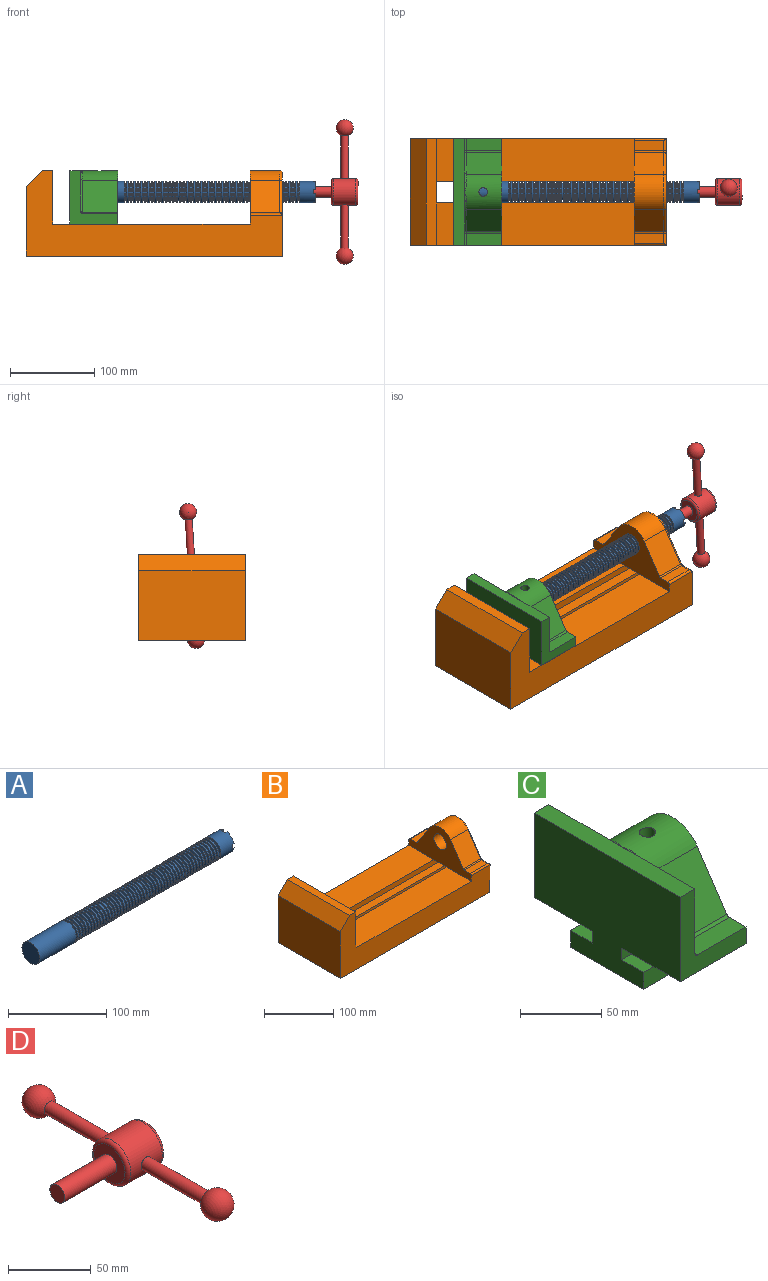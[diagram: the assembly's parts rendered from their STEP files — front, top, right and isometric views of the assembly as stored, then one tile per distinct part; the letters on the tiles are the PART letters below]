
ASSEMBLY  parts=4 mates=3
PART A: 220 faces, bbox 279.4x25.4x25.4 mm
  f0: cylinder r=12.7mm len=25.4mm, axis (-1,0,0), area 1468.2mm2, adj f1,f2,f3,f5,f7,f208,f209,f210
  f1: plane 9.9x9.9mm, normal (1,0,0), area 62.3mm2, adj f0,f4,f213,f216
  f2: plane 9.9x9.9mm, normal (1,0,0), area 62.3mm2, adj f0,f4,f210,f218
  f3: plane 9.9x9.9mm, normal (1,0,0), area 62.3mm2, adj f0,f4,f209,f212
  f4: cylinder r=6.35mm len=25.4mm, axis (1,0,0), area 960.3mm2, adj f1,f2,f3,f5,f6,f208,f209,f210
  f5: plane 9.9x9.9mm, normal (1,0,0), area 62.3mm2, adj f0,f4,f215,f217
  f6: plane 12.7x12.7mm, normal (1,0,0), area 126.7mm2, adj f4
  f7: cone r=12.7mm half-angle=76deg, axis (1,0,0), area 188mm2, adj f0,f9
  f8: cone r=10.16mm half-angle=76deg, axis (-1,0,0), area 188mm2, adj f9,f10
  f9: cylinder r=10.16mm len=20.32mm, axis (1,0,0), area 81.1mm2, adj f7,f8
  f10: cylinder r=12.7mm len=25.4mm, axis (-1,0,0), area 131.7mm2, adj f8,f11
  f11: cone r=12.7mm half-angle=76deg, axis (1,0,0), area 188mm2, adj f10,f13
  f12: cone r=10.16mm half-angle=76deg, axis (-1,0,0), area 188mm2, adj f13,f14
  f13: cylinder r=10.16mm len=20.32mm, axis (1,0,0), area 81.1mm2, adj f11,f12
  f14: cylinder r=12.7mm len=25.4mm, axis (-1,0,0), area 131.7mm2, adj f12,f15
  f15: cone r=12.7mm half-angle=76deg, axis (1,0,0), area 188mm2, adj f14,f17
  f16: cone r=10.16mm half-angle=76deg, axis (-1,0,0), area 188mm2, adj f17,f18
  f17: cylinder r=10.16mm len=20.32mm, axis (1,0,0), area 81.1mm2, adj f15,f16
  f18: cylinder r=12.7mm len=25.4mm, axis (-1,0,0), area 131.7mm2, adj f16,f19
  f19: cone r=12.7mm half-angle=76deg, axis (1,0,0), area 188mm2, adj f18,f21
  f20: cone r=10.16mm half-angle=76deg, axis (-1,0,0), area 188mm2, adj f21,f22
  f21: cylinder r=10.16mm len=20.32mm, axis (1,0,0), area 81.1mm2, adj f19,f20
  f22: cylinder r=12.7mm len=25.4mm, axis (-1,0,0), area 131.7mm2, adj f20,f23
  f23: cone r=12.7mm half-angle=76deg, axis (1,0,0), area 188mm2, adj f22,f25
  f24: cone r=10.16mm half-angle=76deg, axis (-1,0,0), area 188mm2, adj f25,f26
  f25: cylinder r=10.16mm len=20.32mm, axis (1,0,0), area 81.1mm2, adj f23,f24
  f26: cylinder r=12.7mm len=25.4mm, axis (-1,0,0), area 131.7mm2, adj f24,f27
  f27: cone r=12.7mm half-angle=76deg, axis (1,0,0), area 188mm2, adj f26,f29
  f28: cone r=10.16mm half-angle=76deg, axis (-1,0,0), area 188mm2, adj f29,f30
  f29: cylinder r=10.16mm len=20.32mm, axis (1,0,0), area 81.1mm2, adj f27,f28
  f30: cylinder r=12.7mm len=25.4mm, axis (-1,0,0), area 131.7mm2, adj f28,f31
  f31: cone r=12.7mm half-angle=76deg, axis (1,0,0), area 188mm2, adj f30,f33
  f32: cone r=10.16mm half-angle=76deg, axis (-1,0,0), area 188mm2, adj f33,f34
  f33: cylinder r=10.16mm len=20.32mm, axis (1,0,0), area 81.1mm2, adj f31,f32
  f34: cylinder r=12.7mm len=25.4mm, axis (-1,0,0), area 131.7mm2, adj f32,f35
  f35: cone r=12.7mm half-angle=76deg, axis (1,0,0), area 188mm2, adj f34,f37
  f36: cone r=10.16mm half-angle=76deg, axis (-1,0,0), area 188mm2, adj f37,f38
  f37: cylinder r=10.16mm len=20.32mm, axis (1,0,0), area 81.1mm2, adj f35,f36
  f38: cylinder r=12.7mm len=25.4mm, axis (-1,0,0), area 131.7mm2, adj f36,f39
  f39: cone r=12.7mm half-angle=76deg, axis (1,0,0), area 188mm2, adj f38,f41
  f40: cone r=10.16mm half-angle=76deg, axis (-1,0,0), area 188mm2, adj f41,f42
  f41: cylinder r=10.16mm len=20.32mm, axis (1,0,0), area 81.1mm2, adj f39,f40
  f42: cylinder r=12.7mm len=25.4mm, axis (-1,0,0), area 131.7mm2, adj f40,f43
  f43: cone r=12.7mm half-angle=76deg, axis (1,0,0), area 188mm2, adj f42,f45
  f44: cone r=10.16mm half-angle=76deg, axis (-1,0,0), area 188mm2, adj f45,f46
  f45: cylinder r=10.16mm len=20.32mm, axis (1,0,0), area 81.1mm2, adj f43,f44
  f46: cylinder r=12.7mm len=25.4mm, axis (-1,0,0), area 131.7mm2, adj f44,f47
  f47: cone r=12.7mm half-angle=76deg, axis (1,0,0), area 188mm2, adj f46,f49
  f48: cone r=10.16mm half-angle=76deg, axis (-1,0,0), area 188mm2, adj f49,f50
  f49: cylinder r=10.16mm len=20.32mm, axis (1,0,0), area 81.1mm2, adj f47,f48
  f50: cylinder r=12.7mm len=25.4mm, axis (-1,0,0), area 131.7mm2, adj f48,f51
  f51: cone r=12.7mm half-angle=76deg, axis (1,0,0), area 188mm2, adj f50,f53
  f52: cone r=10.16mm half-angle=76deg, axis (-1,0,0), area 188mm2, adj f53,f54
  f53: cylinder r=10.16mm len=20.32mm, axis (1,0,0), area 81.1mm2, adj f51,f52
  f54: cylinder r=12.7mm len=25.4mm, axis (-1,0,0), area 131.7mm2, adj f52,f55
  f55: cone r=12.7mm half-angle=76deg, axis (1,0,0), area 188mm2, adj f54,f57
  f56: cone r=10.16mm half-angle=76deg, axis (-1,0,0), area 188mm2, adj f57,f58
  f57: cylinder r=10.16mm len=20.32mm, axis (1,0,0), area 81.1mm2, adj f55,f56
  f58: cylinder r=12.7mm len=25.4mm, axis (-1,0,0), area 131.7mm2, adj f56,f59
  f59: cone r=12.7mm half-angle=76deg, axis (1,0,0), area 188mm2, adj f58,f61
  f60: cone r=10.16mm half-angle=76deg, axis (-1,0,0), area 188mm2, adj f61,f62
  f61: cylinder r=10.16mm len=20.32mm, axis (1,0,0), area 81.1mm2, adj f59,f60
  f62: cylinder r=12.7mm len=25.4mm, axis (-1,0,0), area 131.7mm2, adj f60,f63
  f63: cone r=12.7mm half-angle=76deg, axis (1,0,0), area 188mm2, adj f62,f65
  f64: cone r=10.16mm half-angle=76deg, axis (-1,0,0), area 188mm2, adj f65,f66
  f65: cylinder r=10.16mm len=20.32mm, axis (1,0,0), area 81.1mm2, adj f63,f64
  f66: cylinder r=12.7mm len=25.4mm, axis (-1,0,0), area 131.7mm2, adj f64,f67
  f67: cone r=12.7mm half-angle=76deg, axis (1,0,0), area 188mm2, adj f66,f69
  f68: cone r=10.16mm half-angle=76deg, axis (-1,0,0), area 188mm2, adj f69,f70
  f69: cylinder r=10.16mm len=20.32mm, axis (1,0,0), area 81.1mm2, adj f67,f68
  f70: cylinder r=12.7mm len=25.4mm, axis (-1,0,0), area 131.7mm2, adj f68,f71
  f71: cone r=12.7mm half-angle=76deg, axis (1,0,0), area 188mm2, adj f70,f73
  f72: cone r=10.16mm half-angle=76deg, axis (-1,0,0), area 188mm2, adj f73,f74
  f73: cylinder r=10.16mm len=20.32mm, axis (1,0,0), area 81.1mm2, adj f71,f72
  f74: cylinder r=12.7mm len=25.4mm, axis (-1,0,0), area 131.7mm2, adj f72,f75
  f75: cone r=12.7mm half-angle=76deg, axis (1,0,0), area 188mm2, adj f74,f77
  f76: cone r=10.16mm half-angle=76deg, axis (-1,0,0), area 188mm2, adj f77,f78
  f77: cylinder r=10.16mm len=20.32mm, axis (1,0,0), area 81.1mm2, adj f75,f76
  f78: cylinder r=12.7mm len=25.4mm, axis (-1,0,0), area 131.7mm2, adj f76,f79
  f79: cone r=12.7mm half-angle=76deg, axis (1,0,0), area 188mm2, adj f78,f81
  f80: cone r=10.16mm half-angle=76deg, axis (-1,0,0), area 188mm2, adj f81,f82
  f81: cylinder r=10.16mm len=20.32mm, axis (1,0,0), area 81.1mm2, adj f79,f80
  f82: cylinder r=12.7mm len=25.4mm, axis (-1,0,0), area 131.7mm2, adj f80,f83
  f83: cone r=12.7mm half-angle=76deg, axis (1,0,0), area 188mm2, adj f82,f85
  f84: cone r=10.16mm half-angle=76deg, axis (-1,0,0), area 188mm2, adj f85,f86
  f85: cylinder r=10.16mm len=20.32mm, axis (1,0,0), area 81.1mm2, adj f83,f84
  f86: cylinder r=12.7mm len=25.4mm, axis (-1,0,0), area 131.7mm2, adj f84,f87
  f87: cone r=12.7mm half-angle=76deg, axis (1,0,0), area 188mm2, adj f86,f89
  f88: cone r=10.16mm half-angle=76deg, axis (-1,0,0), area 188mm2, adj f89,f90
  f89: cylinder r=10.16mm len=20.32mm, axis (1,0,0), area 81.1mm2, adj f87,f88
  f90: cylinder r=12.7mm len=25.4mm, axis (-1,0,0), area 131.7mm2, adj f88,f91
  f91: cone r=12.7mm half-angle=76deg, axis (1,0,0), area 188mm2, adj f90,f93
  f92: cone r=10.16mm half-angle=76deg, axis (-1,0,0), area 188mm2, adj f93,f94
  f93: cylinder r=10.16mm len=20.32mm, axis (1,0,0), area 81.1mm2, adj f91,f92
  f94: cylinder r=12.7mm len=25.4mm, axis (-1,0,0), area 131.7mm2, adj f92,f95
  f95: cone r=12.7mm half-angle=76deg, axis (1,0,0), area 188mm2, adj f94,f97
  f96: cone r=10.16mm half-angle=76deg, axis (-1,0,0), area 188mm2, adj f97,f98
  f97: cylinder r=10.16mm len=20.32mm, axis (1,0,0), area 81.1mm2, adj f95,f96
  f98: cylinder r=12.7mm len=25.4mm, axis (-1,0,0), area 131.7mm2, adj f96,f99
  f99: cone r=12.7mm half-angle=76deg, axis (1,0,0), area 188mm2, adj f98,f101
  f100: cone r=10.16mm half-angle=76deg, axis (-1,0,0), area 188mm2, adj f101,f102
  f101: cylinder r=10.16mm len=20.32mm, axis (1,0,0), area 81.1mm2, adj f99,f100
  f102: cylinder r=12.7mm len=25.4mm, axis (-1,0,0), area 131.7mm2, adj f100,f103
  f103: cone r=12.7mm half-angle=76deg, axis (1,0,0), area 188mm2, adj f102,f105
  f104: cone r=10.16mm half-angle=76deg, axis (-1,0,0), area 188mm2, adj f105,f106
  f105: cylinder r=10.16mm len=20.32mm, axis (1,0,0), area 81.1mm2, adj f103,f104
  f106: cylinder r=12.7mm len=25.4mm, axis (-1,0,0), area 131.7mm2, adj f104,f107
  f107: cone r=12.7mm half-angle=76deg, axis (1,0,0), area 188mm2, adj f106,f109
  f108: cone r=10.16mm half-angle=76deg, axis (-1,0,0), area 188mm2, adj f109,f110
  f109: cylinder r=10.16mm len=20.32mm, axis (1,0,0), area 81.1mm2, adj f107,f108
  f110: cylinder r=12.7mm len=25.4mm, axis (-1,0,0), area 131.7mm2, adj f108,f111
  f111: cone r=12.7mm half-angle=76deg, axis (1,0,0), area 188mm2, adj f110,f113
  f112: cone r=10.16mm half-angle=76deg, axis (-1,0,0), area 188mm2, adj f113,f114
  f113: cylinder r=10.16mm len=20.32mm, axis (1,0,0), area 81.1mm2, adj f111,f112
  f114: cylinder r=12.7mm len=25.4mm, axis (-1,0,0), area 131.7mm2, adj f112,f115
  f115: cone r=12.7mm half-angle=76deg, axis (1,0,0), area 188mm2, adj f114,f117
  f116: cone r=10.16mm half-angle=76deg, axis (-1,0,0), area 188mm2, adj f117,f118
  f117: cylinder r=10.16mm len=20.32mm, axis (1,0,0), area 81.1mm2, adj f115,f116
  f118: cylinder r=12.7mm len=25.4mm, axis (-1,0,0), area 131.7mm2, adj f116,f119
  f119: cone r=12.7mm half-angle=76deg, axis (1,0,0), area 188mm2, adj f118,f121
  f120: cone r=10.16mm half-angle=76deg, axis (-1,0,0), area 188mm2, adj f121,f122
  f121: cylinder r=10.16mm len=20.32mm, axis (1,0,0), area 81.1mm2, adj f119,f120
  f122: cylinder r=12.7mm len=25.4mm, axis (-1,0,0), area 131.7mm2, adj f120,f123
  f123: cone r=12.7mm half-angle=76deg, axis (1,0,0), area 188mm2, adj f122,f125
  f124: cone r=10.16mm half-angle=76deg, axis (-1,0,0), area 188mm2, adj f125,f126
  f125: cylinder r=10.16mm len=20.32mm, axis (1,0,0), area 81.1mm2, adj f123,f124
  f126: cylinder r=12.7mm len=25.4mm, axis (-1,0,0), area 131.7mm2, adj f124,f127
  f127: cone r=12.7mm half-angle=76deg, axis (1,0,0), area 188mm2, adj f126,f129
  f128: cone r=10.16mm half-angle=76deg, axis (-1,0,0), area 188mm2, adj f129,f130
  f129: cylinder r=10.16mm len=20.32mm, axis (1,0,0), area 81.1mm2, adj f127,f128
  f130: cylinder r=12.7mm len=25.4mm, axis (-1,0,0), area 131.7mm2, adj f128,f131
  f131: cone r=12.7mm half-angle=76deg, axis (1,0,0), area 188mm2, adj f130,f133
  f132: cone r=10.16mm half-angle=76deg, axis (-1,0,0), area 188mm2, adj f133,f134
  f133: cylinder r=10.16mm len=20.32mm, axis (1,0,0), area 81.1mm2, adj f131,f132
  f134: cylinder r=12.7mm len=25.4mm, axis (-1,0,0), area 131.7mm2, adj f132,f135
  f135: cone r=12.7mm half-angle=76deg, axis (1,0,0), area 188mm2, adj f134,f137
  f136: cone r=10.16mm half-angle=76deg, axis (-1,0,0), area 188mm2, adj f137,f138
  f137: cylinder r=10.16mm len=20.32mm, axis (1,0,0), area 81.1mm2, adj f135,f136
  f138: cylinder r=12.7mm len=25.4mm, axis (-1,0,0), area 131.7mm2, adj f136,f139
  f139: cone r=12.7mm half-angle=76deg, axis (1,0,0), area 188mm2, adj f138,f141
  f140: cone r=10.16mm half-angle=76deg, axis (-1,0,0), area 188mm2, adj f141,f142
  f141: cylinder r=10.16mm len=20.32mm, axis (1,0,0), area 81.1mm2, adj f139,f140
  f142: cylinder r=12.7mm len=25.4mm, axis (-1,0,0), area 131.7mm2, adj f140,f143
  f143: cone r=12.7mm half-angle=76deg, axis (1,0,0), area 188mm2, adj f142,f145
  f144: cone r=10.16mm half-angle=76deg, axis (-1,0,0), area 188mm2, adj f145,f146
  f145: cylinder r=10.16mm len=20.32mm, axis (1,0,0), area 81.1mm2, adj f143,f144
  f146: cylinder r=12.7mm len=25.4mm, axis (-1,0,0), area 131.7mm2, adj f144,f147
  f147: cone r=12.7mm half-angle=76deg, axis (1,0,0), area 188mm2, adj f146,f149
  f148: cone r=10.16mm half-angle=76deg, axis (-1,0,0), area 188mm2, adj f149,f150
  f149: cylinder r=10.16mm len=20.32mm, axis (1,0,0), area 81.1mm2, adj f147,f148
  f150: cylinder r=12.7mm len=25.4mm, axis (-1,0,0), area 131.7mm2, adj f148,f151
  f151: cone r=12.7mm half-angle=76deg, axis (1,0,0), area 188mm2, adj f150,f153
  f152: cone r=10.16mm half-angle=76deg, axis (-1,0,0), area 188mm2, adj f153,f154
  f153: cylinder r=10.16mm len=20.32mm, axis (1,0,0), area 81.1mm2, adj f151,f152
  f154: cylinder r=12.7mm len=25.4mm, axis (-1,0,0), area 131.7mm2, adj f152,f155
  f155: cone r=12.7mm half-angle=76deg, axis (1,0,0), area 188mm2, adj f154,f157
  f156: cone r=10.16mm half-angle=76deg, axis (-1,0,0), area 188mm2, adj f157,f158
  f157: cylinder r=10.16mm len=20.32mm, axis (1,0,0), area 81.1mm2, adj f155,f156
  f158: cylinder r=12.7mm len=25.4mm, axis (-1,0,0), area 131.7mm2, adj f156,f159
  f159: cone r=12.7mm half-angle=76deg, axis (1,0,0), area 188mm2, adj f158,f161
  f160: cone r=10.16mm half-angle=76deg, axis (-1,0,0), area 188mm2, adj f161,f162
  f161: cylinder r=10.16mm len=20.32mm, axis (1,0,0), area 81.1mm2, adj f159,f160
  f162: cylinder r=12.7mm len=25.4mm, axis (-1,0,0), area 131.7mm2, adj f160,f163
  f163: cone r=12.7mm half-angle=76deg, axis (1,0,0), area 188mm2, adj f162,f165
  f164: cone r=10.16mm half-angle=76deg, axis (-1,0,0), area 188mm2, adj f165,f166
  f165: cylinder r=10.16mm len=20.32mm, axis (1,0,0), area 81.1mm2, adj f163,f164
  f166: cylinder r=12.7mm len=25.4mm, axis (-1,0,0), area 131.7mm2, adj f164,f167
  f167: cone r=12.7mm half-angle=76deg, axis (1,0,0), area 188mm2, adj f166,f169
  f168: cone r=10.16mm half-angle=76deg, axis (-1,0,0), area 188mm2, adj f169,f170
  f169: cylinder r=10.16mm len=20.32mm, axis (1,0,0), area 81.1mm2, adj f167,f168
  f170: cylinder r=12.7mm len=25.4mm, axis (-1,0,0), area 131.7mm2, adj f168,f171
  f171: cone r=12.7mm half-angle=76deg, axis (1,0,0), area 188mm2, adj f170,f173
  f172: cone r=10.16mm half-angle=76deg, axis (-1,0,0), area 188mm2, adj f173,f174
  f173: cylinder r=10.16mm len=20.32mm, axis (1,0,0), area 81.1mm2, adj f171,f172
  f174: cylinder r=12.7mm len=25.4mm, axis (-1,0,0), area 131.7mm2, adj f172,f175
  f175: cone r=12.7mm half-angle=76deg, axis (1,0,0), area 188mm2, adj f174,f177
  f176: cone r=10.16mm half-angle=76deg, axis (-1,0,0), area 188mm2, adj f177,f178
  f177: cylinder r=10.16mm len=20.32mm, axis (1,0,0), area 81.1mm2, adj f175,f176
  f178: cylinder r=12.7mm len=25.4mm, axis (-1,0,0), area 131.7mm2, adj f176,f179
  f179: cone r=12.7mm half-angle=76deg, axis (1,0,0), area 188mm2, adj f178,f181
  f180: cone r=10.16mm half-angle=76deg, axis (-1,0,0), area 188mm2, adj f181,f182
  f181: cylinder r=10.16mm len=20.32mm, axis (1,0,0), area 81.1mm2, adj f179,f180
  f182: cylinder r=12.7mm len=25.4mm, axis (-1,0,0), area 131.7mm2, adj f180,f183
  f183: cone r=12.7mm half-angle=76deg, axis (1,0,0), area 188mm2, adj f182,f185
  f184: cone r=10.16mm half-angle=76deg, axis (-1,0,0), area 188mm2, adj f185,f186
  f185: cylinder r=10.16mm len=20.32mm, axis (1,0,0), area 81.1mm2, adj f183,f184
  f186: cylinder r=12.7mm len=25.4mm, axis (-1,0,0), area 131.7mm2, adj f184,f187
  f187: cone r=12.7mm half-angle=76deg, axis (1,0,0), area 188mm2, adj f186,f189
  f188: cone r=10.16mm half-angle=76deg, axis (-1,0,0), area 188mm2, adj f189,f190
  f189: cylinder r=10.16mm len=20.32mm, axis (1,0,0), area 81.1mm2, adj f187,f188
  f190: cylinder r=12.7mm len=25.4mm, axis (-1,0,0), area 131.7mm2, adj f188,f191
  f191: cone r=12.7mm half-angle=76deg, axis (1,0,0), area 188mm2, adj f190,f193
  f192: cone r=10.16mm half-angle=76deg, axis (-1,0,0), area 188mm2, adj f193,f194
  f193: cylinder r=10.16mm len=20.32mm, axis (1,0,0), area 81.1mm2, adj f191,f192
  f194: cylinder r=12.7mm len=25.4mm, axis (-1,0,0), area 131.7mm2, adj f192,f195
  f195: cone r=12.7mm half-angle=76deg, axis (1,0,0), area 188mm2, adj f194,f197
  f196: cone r=10.16mm half-angle=76deg, axis (-1,0,0), area 188mm2, adj f197,f198
  f197: cylinder r=10.16mm len=20.32mm, axis (1,0,0), area 81.1mm2, adj f195,f196
  f198: cylinder r=12.7mm len=25.4mm, axis (-1,0,0), area 131.7mm2, adj f196,f199
  f199: cone r=12.7mm half-angle=76deg, axis (1,0,0), area 188mm2, adj f198,f201
  f200: cone r=10.16mm half-angle=76deg, axis (-1,0,0), area 188mm2, adj f201,f202
  f201: cylinder r=10.16mm len=20.32mm, axis (1,0,0), area 81.1mm2, adj f199,f200
  f202: cylinder r=12.7mm len=25.4mm, axis (-1,0,0), area 131.7mm2, adj f200,f203
  f203: cone r=12.7mm half-angle=76deg, axis (1,0,0), area 188mm2, adj f202,f205
  f204: cone r=10.16mm half-angle=76deg, axis (-1,0,0), area 188mm2, adj f205,f207
  f205: cylinder r=10.16mm len=20.32mm, axis (1,0,0), area 81.1mm2, adj f203,f204
  f206: plane 25.4x25.4mm, normal (-1,0,0), area 506.7mm2, adj f207
  f207: cylinder r=12.7mm len=52.45mm, axis (-1,0,0), area 4185.4mm2, adj f204,f206
  f208: plane 6.88x5.08mm, normal (1,0,0), area 32.7mm2, adj f0,f4,f209,f210
  f209: plane 6.62x2.54mm, normal (0,-1,0), area 16.8mm2, adj f0,f3,f4,f208
  f210: plane 6.62x2.54mm, normal (0,1,0), area 16.8mm2, adj f0,f2,f4,f208
  f211: plane 6.88x5.08mm, normal (1,0,0), area 32.7mm2, adj f0,f4,f212,f213
  f212: plane 6.62x2.54mm, normal (0,0,1), area 16.8mm2, adj f0,f3,f4,f211
  f213: plane 6.62x2.54mm, normal (0,0,-1), area 16.8mm2, adj f0,f1,f4,f211
  f214: plane 6.88x5.08mm, normal (1,0,0), area 32.7mm2, adj f0,f4,f215,f216
  f215: plane 6.62x2.54mm, normal (0,1,0), area 16.8mm2, adj f0,f4,f5,f214
  f216: plane 6.62x2.54mm, normal (0,-1,0), area 16.8mm2, adj f0,f1,f4,f214
  f217: plane 6.62x2.54mm, normal (0,0,-1), area 16.8mm2, adj f0,f4,f5,f219
  f218: plane 6.62x2.54mm, normal (0,0,1), area 16.8mm2, adj f0,f2,f4,f219
  f219: plane 6.88x5.08mm, normal (1,0,0), area 32.7mm2, adj f0,f4,f217,f218
PART B: 39 faces, bbox 304.8x127x103.7 mm
  f0: plane 234.95x50.8mm, normal (0,0,1), area 11935.5mm2, adj f3,f8,f16,f26
  f1: plane 127x99.06mm, normal (1,0,0), area 7097.5mm2, adj f7,f8,f9,f14,f17,f18,f19,f20
  f2: plane 234.95x50.8mm, normal (0,0,1), area 11935.5mm2, adj f3,f9,f16,f27
  f3: plane 127x101.6mm, normal (1,0,0), area 9516.1mm2, adj f0,f2,f4,f7,f8,f9,f18,f19
  f4: plane 127x12.7mm, normal (0,0,1), area 1612.9mm2, adj f3,f5,f8,f9
  f5: plane 127x19.05mm, normal (-0.71,0,0.71), area 3421.5mm2, adj f4,f6,f8,f9
  f6: plane 127x82.55mm, normal (-1,0,0), area 10483.8mm2, adj f5,f7,f8,f9
  f7: plane 304.8x127mm, normal (0,0,-1), area 31774.1mm2, adj f1,f3,f6,f8,f9,f21,f22
  f8: plane 304.8x101.6mm, normal (0,-1,0), area 13834.6mm2, adj f0,f1,f3,f4,f5,f6,f7,f16
  f9: plane 304.8x101.6mm, normal (0,1,0), area 13834.6mm2, adj f1,f2,f3,f4,f5,f6,f7,f16
  f10: plane 35.56x11.98mm, normal (0,0,1), area 426mm2, adj f16,f28,f29,f30
  f11: plane 38.43x35.56mm, normal (0,0.83,0.56), area 1645.4mm2, adj f12,f16,f29,f32
  f12: cylinder r=25.4mm len=42.19mm, axis (1,0,0), area 1770.2mm2, adj f11,f13,f16,f33
  f13: plane 38.43x35.56mm, normal (0,-0.83,0.56), area 1645.4mm2, adj f12,f16,f34,f35
  f14: cylinder r=12.7mm len=38.1mm, axis (1,0,0), area 3040.2mm2, adj f1,f16
  f15: plane 35.56x11.98mm, normal (0,0,1), area 426mm2, adj f16,f34,f36,f38
  f16: plane 127x63.5mm, normal (-1,0,0), area 4155.5mm2, adj f0,f2,f8,f9,f10,f11,f12,f13
  f17: plane 38.1x25.4mm, normal (0,0,-1), area 967.7mm2, adj f1,f16,f26,f27
  f18: plane 273.05x19.05mm, normal (0,0,-1), area 5201.6mm2, adj f1,f3,f19,f26
  f19: plane 273.05x12.7mm, normal (0,1,0), area 3467.7mm2, adj f1,f3,f18,f20
  f20: plane 273.05x19.05mm, normal (0,0,1), area 5201.6mm2, adj f1,f3,f19,f21
  f21: plane 273.05x16.51mm, normal (0,1,0), area 4508.1mm2, adj f1,f3,f7,f20
  f22: plane 273.05x16.51mm, normal (0,-1,0), area 4508.1mm2, adj f1,f3,f7,f23
  f23: plane 273.05x19.05mm, normal (0,0,1), area 5201.6mm2, adj f1,f3,f22,f24
  f24: plane 273.05x12.7mm, normal (0,-1,0), area 3467.7mm2, adj f1,f3,f23,f25
  f25: plane 273.05x19.05mm, normal (0,0,-1), area 5201.6mm2, adj f1,f3,f24,f27
  f26: plane 273.05x8.89mm, normal (0,1,0), area 2427.4mm2, adj f0,f1,f3,f17,f18
  f27: plane 273.05x8.89mm, normal (0,-1,0), area 2427.4mm2, adj f1,f2,f3,f17,f25
  f28: cylinder r=2.54mm len=38.1mm, axis (1,0,0), area 148.3mm2, adj f9,f10,f16,f30
  f29: cylinder r=2.54mm len=35.56mm, axis (-1,0,0), area 88.5mm2, adj f10,f11,f16,f31
  f30: cylinder r=2.54mm len=14.52mm, axis (0,1,0), area 54.3mm2, adj f1,f10,f28,f31
  f31: torus R=5.08mm, axis (-1,0,0), area 13.5mm2, adj f1,f29,f30,f32
  f32: cylinder r=2.54mm len=39.84mm, axis (0,0.56,-0.83), area 184.6mm2, adj f1,f11,f31,f33
  f33: torus R=22.86mm, axis (-1,0,0), area 191.4mm2, adj f1,f12,f32,f35
  f34: cylinder r=2.54mm len=35.56mm, axis (-1,0,0), area 88.5mm2, adj f13,f15,f16,f37
  f35: cylinder r=2.54mm len=39.84mm, axis (0,0.56,0.83), area 184.6mm2, adj f1,f13,f33,f37
  f36: cylinder r=2.54mm len=38.1mm, axis (-1,0,0), area 148.3mm2, adj f8,f15,f16,f38
  f37: torus R=5.08mm, axis (-1,0,0), area 13.5mm2, adj f1,f34,f35,f38
  f38: cylinder r=2.54mm len=14.52mm, axis (0,1,0), area 54.3mm2, adj f1,f15,f36,f37
PART C: 36 faces, bbox 57.2x127x89 mm
  f0: plane 57.15x50.8mm, normal (0,0,-1), area 2903.2mm2, adj f6,f9,f10,f23
  f1: cylinder r=12.7mm len=44.45mm, axis (1,0,0), area 3464.3mm2, adj f6,f15,f16
  f2: plane 41.91x14.52mm, normal (0,0,1), area 608.5mm2, adj f6,f11,f24,f25
  f3: plane 51.86x48.26mm, normal (1,0,0), area 1495.7mm2, adj f8,f10,f31,f33,f35
  f4: plane 51.86x48.26mm, normal (1,0,0), area 1495.7mm2, adj f8,f11,f24,f28,f29
  f5: plane 57.15x50.8mm, normal (0,0,-1), area 2903.2mm2, adj f6,f9,f11,f22
  f6: plane 127x85.09mm, normal (1,0,0), area 5190.6mm2, adj f0,f1,f2,f5,f7,f10,f11,f12
  f7: plane 41.91x14.52mm, normal (0,0,1), area 608.5mm2, adj f6,f10,f30,f31
  f8: plane 127x12.7mm, normal (0,0,1), area 1612.9mm2, adj f3,f4,f9,f10,f11,f26,f34
  f9: plane 127x85.09mm, normal (-1,0,0), area 9096.8mm2, adj f0,f5,f8,f10,f11,f17,f18,f19
  f10: plane 63.5x57.15mm, normal (0,-1,0), area 1372.3mm2, adj f0,f3,f6,f7,f8,f9,f31
  f11: plane 63.5x57.15mm, normal (0,1,0), area 1372.3mm2, adj f2,f4,f5,f6,f8,f9,f24
  f12: plane 41.91x38.43mm, normal (0,-0.83,0.56), area 1939.2mm2, adj f6,f13,f30,f33
  f13: cylinder r=25.4mm len=44.45mm, axis (1,0,0), area 2026.5mm2, adj f6,f12,f14,f16,f26,f28,f34,f35
  f14: plane 41.91x38.43mm, normal (0,0.83,0.56), area 1939.2mm2, adj f6,f13,f25,f29
  f15: plane 25.4x25.4mm, normal (1,0,0), area 506.7mm2, adj f1
  f16: cylinder r=5.08mm len=13.76mm, axis (0,0,1), area 414mm2, adj f1,f13
  f17: plane 57.15x19.05mm, normal (0,0,1), area 1088.7mm2, adj f6,f9,f18,f23
  f18: plane 57.15x12.7mm, normal (0,-1,0), area 725.8mm2, adj f6,f9,f17,f19
  f19: plane 63.5x57.15mm, normal (0,0,-1), area 3629mm2, adj f6,f9,f18,f20
  f20: plane 57.15x12.7mm, normal (0,1,0), area 725.8mm2, adj f6,f9,f19,f21
  f21: plane 57.15x19.05mm, normal (0,0,1), area 1088.7mm2, adj f6,f9,f20,f22
  f22: plane 57.15x8.89mm, normal (0,1,0), area 508.1mm2, adj f5,f6,f9,f21
  f23: plane 57.15x8.89mm, normal (0,-1,0), area 508.1mm2, adj f0,f6,f9,f17
  f24: cylinder r=2.54mm len=14.52mm, axis (0,-1,0), area 57.9mm2, adj f2,f4,f11,f27
  f25: cylinder r=2.54mm len=41.91mm, axis (1,0,0), area 104.3mm2, adj f2,f6,f14,f27
  f26: bspline ~12.24x2.8mm, area 20.9mm2, adj f8,f13,f28
  f27: sphere r=2.54mm, area 6.3mm2, adj f24,f25,f29
  f28: torus R=27.94mm, axis (1,0,0), area 57.8mm2, adj f4,f13,f26,f29
  f29: cylinder r=2.54mm len=39.84mm, axis (0,-0.56,0.83), area 184.6mm2, adj f4,f14,f27,f28
  f30: cylinder r=2.54mm len=41.91mm, axis (1,0,0), area 104.3mm2, adj f6,f7,f12,f32
  f31: cylinder r=2.54mm len=14.52mm, axis (0,-1,0), area 57.9mm2, adj f3,f7,f10,f32
  f32: sphere r=2.54mm, area 6.3mm2, adj f30,f31,f33
  f33: cylinder r=2.54mm len=39.84mm, axis (0,-0.56,-0.83), area 184.6mm2, adj f3,f12,f32,f35
  f34: bspline ~12.24x2.8mm, area 20.9mm2, adj f8,f13,f35
  f35: torus R=27.94mm, axis (1,0,0), area 57.8mm2, adj f3,f13,f33,f34
PART D: 11 faces, bbox 76.2x172.7x34.4 mm
  f0: sphere r=10.16mm, area 1231.8mm2, adj f1
  f1: cylinder r=4.45mm len=51.82mm, axis (0,1,0), area 1438.5mm2, adj f0,f4
  f2: sphere r=10.16mm, area 1231.8mm2, adj f3
  f3: cylinder r=4.45mm len=51.82mm, axis (0,1,0), area 1438.5mm2, adj f2,f4
  f4: cylinder r=15.88mm len=31.75mm, axis (-1,0,0), area 2534.7mm2, adj f1,f3,f9,f10
  f5: cylinder r=6.35mm len=44.45mm, axis (-1,0,0), area 1773.5mm2, adj f6,f8
  f6: plane 12.7x12.7mm, normal (-1,0,0), area 126.7mm2, adj f5
  f7: plane 26.67x26.67mm, normal (1,0,0), area 558.6mm2, adj f10
  f8: plane 26.67x26.67mm, normal (-1,0,0), area 432mm2, adj f5,f9
  f9: torus R=13.33mm, axis (1,0,0), area 374.8mm2, adj f4,f8
  f10: torus R=13.33mm, axis (1,0,0), area 374.8mm2, adj f4,f7
PLACE A rot(axis=(1,0,0),86.5deg) t=(20.46,76.05,71.48)mm
PLACE B at identity fixed
PLACE C t=(20.46,0,0)mm
PLACE D rot(axis=(1,0,0),86.5deg) t=(20.46,76.05,71.48)mm
MATE fastened A.f4 <-> D.f5  axis (1,0,0) through (14.11,0,76.2)mm
MATE revolute C.f28 <-> A.f7  axis (1,0,0) through (-239.89,0,76.2)mm
MATE slider B.f3 <-> C.f9  axis (-1,0,0) through (-273.05,-63.5,38.1)mm
